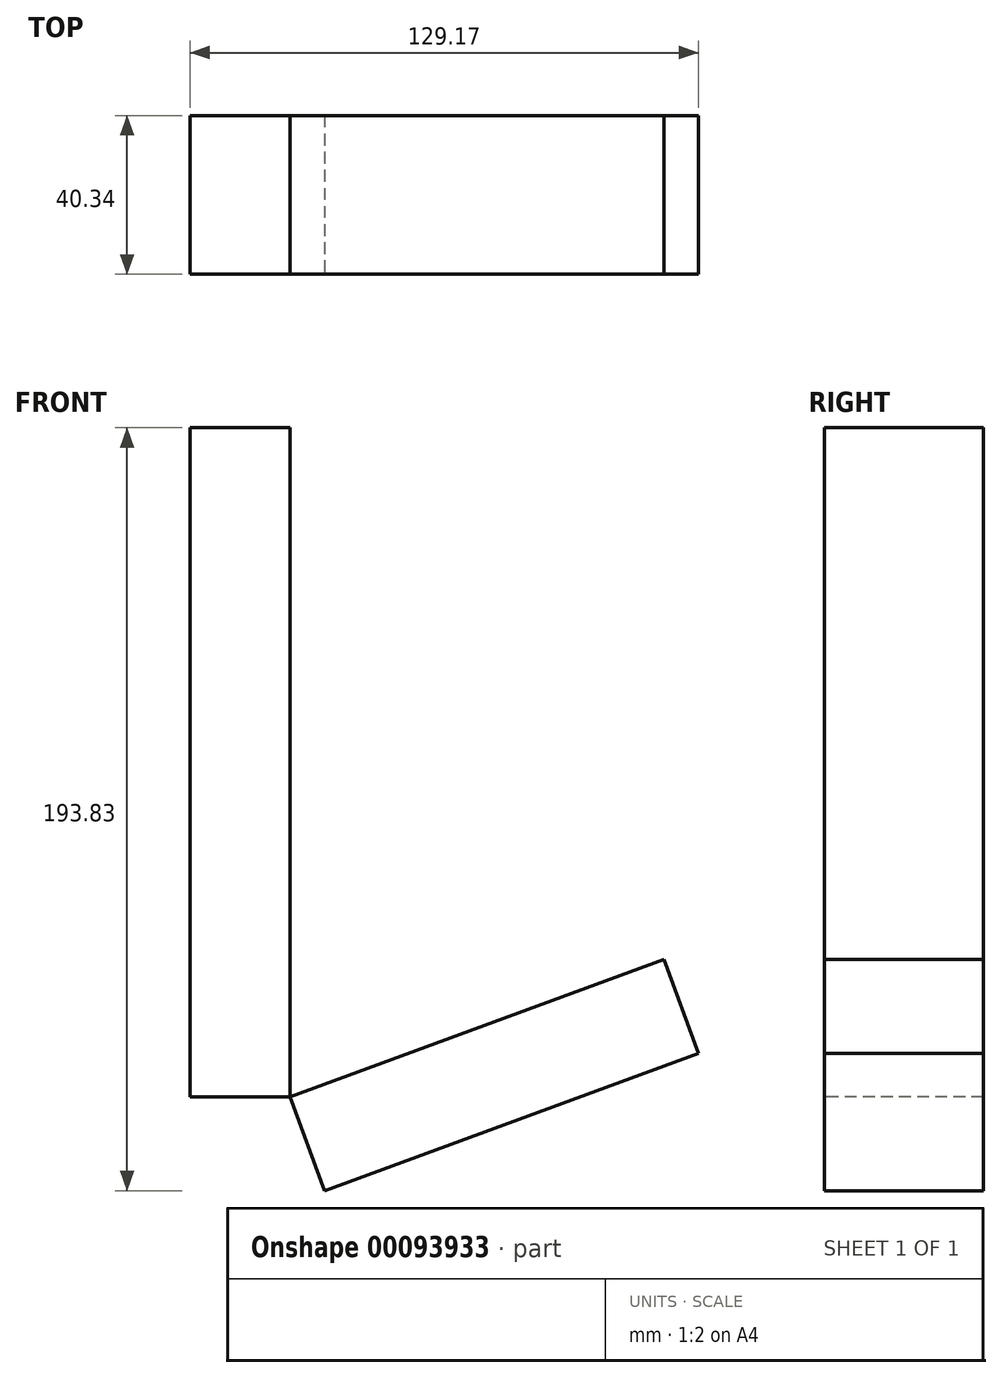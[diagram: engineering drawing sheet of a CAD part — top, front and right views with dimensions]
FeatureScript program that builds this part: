
annotation { "Feature Type Name" : "Feature", "Feature Type Description" : "" }
export const myFeature = defineFeature(function(context is Context, id is Id, definition is map)
    precondition{}
    {
        {
            var Q0;
            Q0=qCreatedBy(makeId("Front.planeOp"),FACE);
            var sketch = newSketch(context, id + "F0", { "sketchPlane" : qUnion([Q0])});
            skLineSegment(sketch, "E0", {"start": v(-57.5, 94.41) * mm, "end": v(-57.5, -75.57) * mm});
            skLineSegment(sketch, "E1", {"start": v(-57.5, -75.57) * mm, "end": v(37.5, -40.68) * mm});
            skSolve(sketch);
        }
        {
            var Q0;
            Q0=sQuery(id+"F0.wireOp",EDGE,"E1");
            var Q1;
            Q1=sQuery(id+"F0.wireOp",EDGE,"E0");
            extrude(context, id + "F1", {"bodyType" : ToolBodyType.SURFACE, "surfaceEntities" : qUnion([Q0, Q1]), "depth" : 40.34 * mm});
        }
        {
            var Q0;
            Q0=makeQuery(id+"F1.opExtrude","SWEPT_FACE",FACE,{"disambiguationData":[OSD([sQuery(id+"F0.wireOp",EDGE,"E1")])]});
            extrude(context, id + "F2", {"entities" : qUnion([Q0]), "depth" : 25.4 * mm});
        }
        {
            var Q0;
            Q0=makeQuery(id+"F1.opExtrude","SWEPT_FACE",FACE,{"disambiguationData":[OSD([sQuery(id+"F0.wireOp",EDGE,"E0")])]});
            extrude(context, id + "F3", {"entities" : qUnion([Q0]), "depth" : 25.4 * mm});
        }
    });
